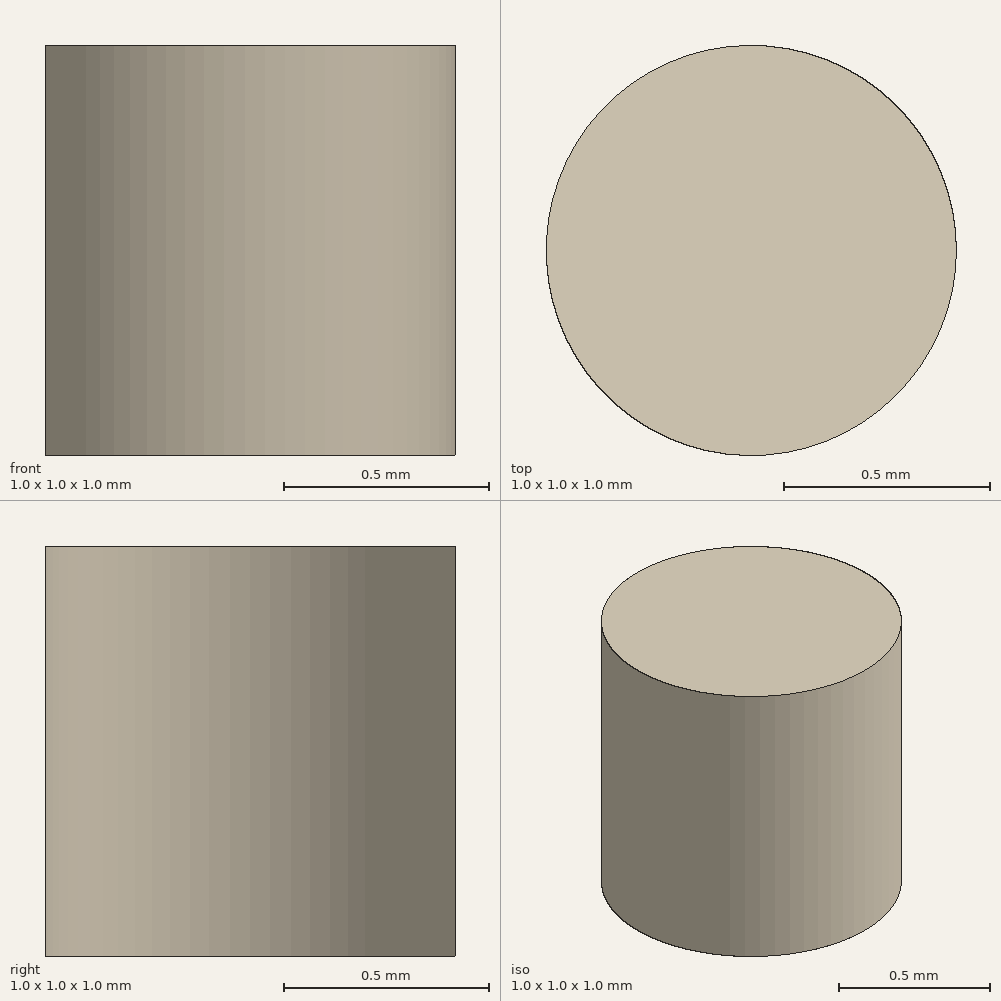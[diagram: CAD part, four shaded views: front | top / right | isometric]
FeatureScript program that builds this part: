
annotation { "Feature Type Name" : "Feature", "Feature Type Description" : "" }
export const myFeature = defineFeature(function(context is Context, id is Id, definition is map)
    precondition{}
    {
        {
            var Q0;
            Q0=qCreatedBy(makeId("Top.planeOp"),FACE);
            var sketch = newSketch(context, id + "F0", { "sketchPlane" : qUnion([Q0])});
            skCircle(sketch, "E0", {"center": v(0, 0) * mm, "radius": 0.5 * mm});
            skSolve(sketch);
        }
        {
            var Q0;
            Q0 = qSketchRegion(id + "F0", true);
            extrude(context, id + "F1", {"entities" : qUnion([Q0]), "depth" : 1 * mm, "offsetDistance" : 25 * mm});
        }
    });
